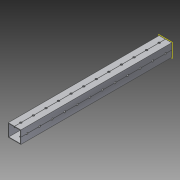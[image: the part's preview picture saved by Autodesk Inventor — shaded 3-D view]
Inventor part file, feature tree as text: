
AUTODESK INVENTOR PART (.ipt)
format: ipt  version: 2014 SP1 (Build 180222100, 222)  size: 1,199,104 bytes
history: native  units: in
note: dims shown in document units (in); Inventor stores cm internally (conversion verified against a paired STEP export)
features: pattern_circular x1, other x1, plane x1, extrude x1, imported_body x1, sketch x1
ambient origin geometry x8: Origin, YZ Plane, XZ Plane, XY Plane, X Axis, Y Axis, Z Axis, Center Point
bodies: Body1 (feature_tree)
feature tree (6):
  pattern_circular  "CirPattern2"
  other  "217-3426-STEP1"
  plane  "Work Plane1"
  extrude  "Extrusion1"  Depth=3937.0079in TaperAngle=0.0deg
  imported_body  "Base1"
  sketch  "Sketch1"  dims[d0=-12.0in d1=3937.0079in d2=0.0in]
